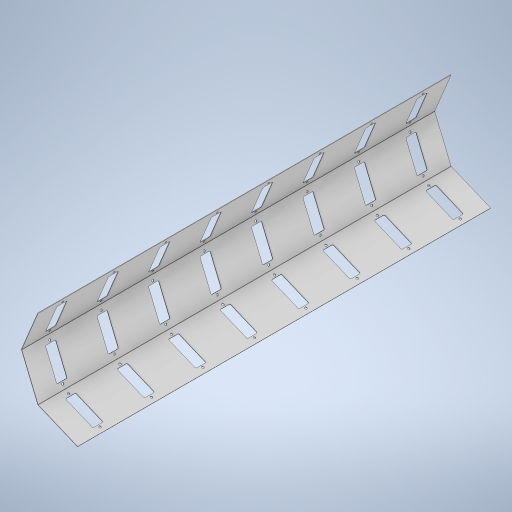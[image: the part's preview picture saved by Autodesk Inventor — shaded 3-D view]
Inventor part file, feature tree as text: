
AUTODESK INVENTOR PART (.ipt)
format: ipt  version: 2024.2 (Build 282272000, 272)  size: 756,224 bytes
history: native  units: mm
features: sheet_metal_op x3, sketch x2, other x2, extrude x1, fillet x1, pattern_circular x1, pattern_linear x1, chamfer x1, projected_geometry x1
ambient origin geometry x8: Origin, YZ Plane, XZ Plane, XY Plane, X Axis, Y Axis, Z Axis, Center Point
bodies: Body1 (feature_tree)
feature tree (13):
  sheet_metal_op  "Contour Flange3"
  extrude  "Extrusion4"  Depth=4.0mm
  fillet  "Fillet1"  Radius=0.9mm
  pattern_circular  "Circular Pattern2"  [2 undecoded]
  pattern_linear  "Rectangular Pattern2"  Spacing1=2.0mm  [1 undecoded]
  chamfer  "Corner Round1"
  sketch  "Sketch2"  dims[d58=4.0mm d59=4.0mm d70=0.9mm]
  other  "Plate6"
  sheet_metal_op  "Bend6"
  sheet_metal_op  "Corner6"
  sketch  "Sketch11"  dims[d72=0.9mm d74=506.0mm d75=2.0mm d76=2.0mm d77=1.0mm d78=4.0mm d79=2.0mm d80=2006.0mm d81=2.0mm d82=3.0mm d83=8.0mm d84=2.0mm d85=2.0mm d141=50.0mm d142=145.0mm d143=10.0mm d145=125.0mm d146=10.0mm d147=10.0mm d148=0.0mm d149=5.0mm d150=30.0mm d151=90.0deg d153=80.0mm d155=250.0mm d156=2.0mm]
  projected_geometry  "Projected Loop1"
  other  "Definition1"
note: 3 required parameter values undecoded (feature->parameter linkage not recoverable at this tier; creation-order binding heuristic only, values carry confidence <= 0.55)
